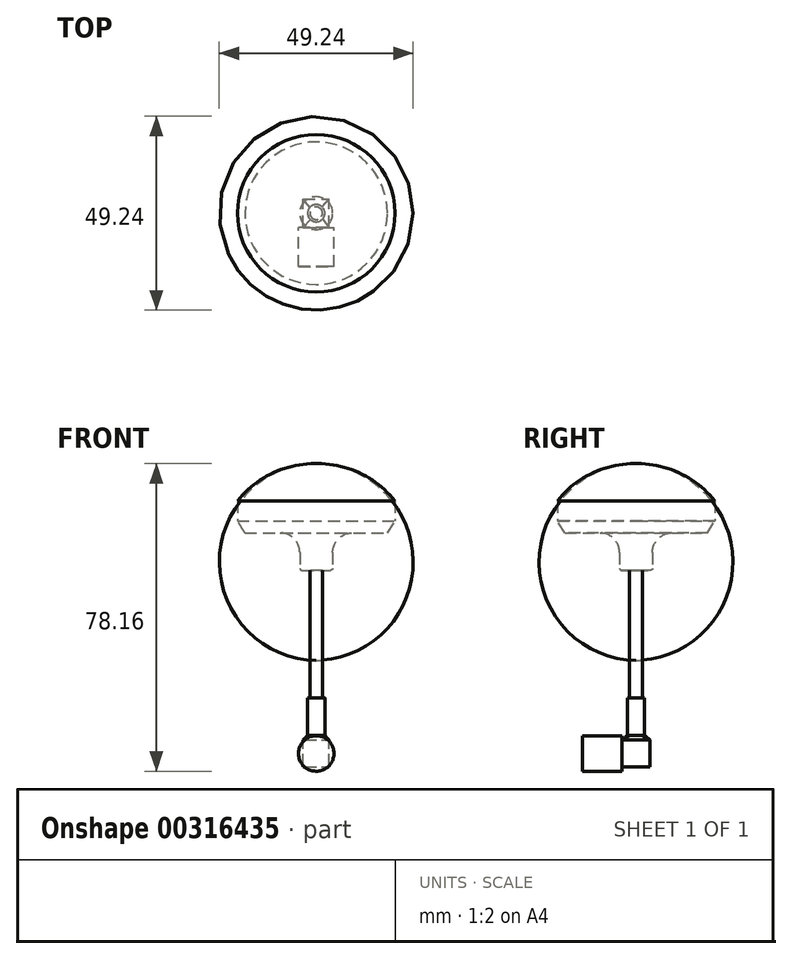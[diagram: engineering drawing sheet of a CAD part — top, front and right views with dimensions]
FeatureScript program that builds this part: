
annotation { "Feature Type Name" : "Feature", "Feature Type Description" : "" }
export const myFeature = defineFeature(function(context is Context, id is Id, definition is map)
    precondition{}
    {
        {
            var Q0;
            Q0=qCreatedBy(makeId("Right.planeOp"),FACE);
            var sketch = newSketch(context, id + "F0", { "sketchPlane" : qUnion([Q0])});
            skLineSegment(sketch, "E0", {"start": v(18.1, 0) * mm, "end": v(9.17, 0) * mm});
            skLineSegment(sketch, "E1", {"start": v(4.17, -5) * mm, "end": v(4.17, -9) * mm});
            skLineSegment(sketch, "E2", {"start": v(3.68, -9.5) * mm, "end": v(0, -9.5) * mm});
            skLineSegment(sketch, "E3", {"start": v(0, -9.5) * mm, "end": v(0, 17.6) * mm});
            skPoint(sketch, "E4.visualSharp", {"position": v(4.17, 0) * mm});
            skArc(sketch, "E4.filletArc", {"start": v(9.17, 0) * mm, "mid": v(5.64, -1.46) * mm, "end": v(4.17, -5) * mm});
            skLineSegment(sketch, "E5", {"start": v(18.1, 0) * mm, "end": v(20, 3) * mm});
            skLineSegment(sketch, "E6", {"start": v(20, 3) * mm, "end": v(20, 8.1) * mm});
            skArc(sketch, "E7", {"start": v(20, 8.1) * mm, "mid": v(11.1, 15.18) * mm, "end": v(0, 17.6) * mm});
            skPoint(sketch, "E8.visualSharp", {"position": v(4.17, -9.5) * mm});
            skArc(sketch, "E8.filletArc", {"start": v(3.68, -9.5) * mm, "mid": v(4.03, -9.35) * mm, "end": v(4.17, -9) * mm});
            skSolve(sketch);
        }
        {
            var Q0;
            Q0 = qSketchRegion(id + "F0", true);
            var Q1;
            Q1=sQuery(id+"F0.wireOp",EDGE,"E3");
            revolve(context, id + "F1", {"entities" : qUnion([Q0]), "axis" : qUnion([Q1]), "revolveType" : RevolveType.FULL});
        }
        {
            var Q0;
            Q0=makeQuery(id+"F1.opRevolve","SWEPT_FACE",FACE,{"disambiguationData":[OSD([sQuery(id+"F0.wireOp",EDGE,"E2")])]});
            var sketch = newSketch(context, id + "F2", { "sketchPlane" : qUnion([Q0])});
            skCircle(sketch, "E9", {"center": v(0, 0) * mm, "radius": 1.6 * mm});
            skSolve(sketch);
        }
        {
            var Q0;
            Q0 = qSketchRegion(id + "F2", true);
            extrude(context, id + "F3", {"entities" : qUnion([Q0]), "operationType" : NewBodyOperationType.ADD, "depth" : 32.4 * mm});
        }
        {
            var Q0;
            Q0=makeQuery(id+"F3.opExtrude","CAP_FACE",FACE,{"disambiguationData":[OSD([sQuery(id+"F2.wireOp",EDGE,"E9")])],"isStart":false});
            var sketch = newSketch(context, id + "F4", { "sketchPlane" : qUnion([Q0])});
            skCircle(sketch, "E10", {"center": v(0, 0) * mm, "radius": 2.2 * mm});
            skSolve(sketch);
        }
        {
            var Q0;
            Q0 = qSketchRegion(id + "F4", true);
            extrude(context, id + "F5", {"entities" : qUnion([Q0]), "operationType" : NewBodyOperationType.ADD, "depth" : 9.5 * mm});
        }
        {
            var Q0;
            Q0=makeQuery(id+"F5.opExtrude","CAP_FACE",FACE,{"disambiguationData":[OSD([sQuery(id+"F4.wireOp",EDGE,"E10")])],"isStart":false});
            cPlane(context, id + "F6", {"entities" : qUnion([Q0]), "cplaneType" : CPlaneType.OFFSET, "offset" : 1.25 * mm, "width" : 150 * mm, "height" : 150 * mm});
        }
        {
            var Q0;
            Q0=qCreatedBy(id+"F6.planeOp",FACE);
            var sketch = newSketch(context, id + "F7", { "sketchPlane" : qUnion([Q0])});
            skLineSegment(sketch, "E11.bottom", {"start": v(-3.3, 3.6) * mm, "end": v(3.3, 3.6) * mm});
            skLineSegment(sketch, "E11.top", {"start": v(-3.3, -3.6) * mm, "end": v(3.3, -3.6) * mm});
            skLineSegment(sketch, "E11.left", {"start": v(-3.3, 3.6) * mm, "end": v(-3.3, -3.6) * mm});
            skLineSegment(sketch, "E11.right", {"start": v(3.3, 3.6) * mm, "end": v(3.3, -3.6) * mm});
            skPoint(sketch, "E11.middle", {"position": v(0, 0) * mm});
            skSolve(sketch);
        }
        {
            var Q0;
            Q0 = qSketchRegion(id + "F7", true);
            extrude(context, id + "F8", {"entities" : qUnion([Q0]), "operationType" : NewBodyOperationType.ADD, "depth" : 6.8 * mm});
        }
        {
            var Q2;
            Q2=makeQuery(id+"F5.opExtrude","CAP_FACE",FACE,{"disambiguationData":[OSD([sQuery(id+"F4.wireOp",EDGE,"E10")])],"isStart":false});
            var Q3;
            Q3=makeQuery(id+"F8.opExtrude","CAP_FACE",FACE,{"disambiguationData":[OSD([sQuery(id+"F7.wireOp",EDGE,"E11.bottom"),sQuery(id+"F7.wireOp",EDGE,"E11.top"),sQuery(id+"F7.wireOp",EDGE,"E11.left"),sQuery(id+"F7.wireOp",EDGE,"E11.right")])],"isStart":true});
            loft(context, id + "F9", {"operationType" : NewBodyOperationType.ADD, "sheetProfilesArray" : [{ "sheetProfileEntities" : qUnion([Q2]) }, { "sheetProfileEntities" : qUnion([Q3]) }]});
        }
        {
            var Q0;
            Q0=makeQuery(id+"F8.opExtrude","SWEPT_FACE",FACE,{"disambiguationData":[OSD([sQuery(id+"F7.wireOp",EDGE,"E11.bottom")])]});
            var sketch = newSketch(context, id + "F10", { "sketchPlane" : qUnion([Q0])});
            skCircle(sketch, "E12", {"center": v(0, -56.05) * mm, "radius": 4.5 * mm});
            skLineSegment(sketch, "E13", {"start": v(0, -56.05) * mm, "end": v(0, -59.45) * mm, "construction": true});
            skLineSegment(sketch, "E14", {"start": v(0, -56.05) * mm, "end": v(0, -52.65) * mm, "construction": true});
            skSolve(sketch);
        }
        {
            var Q0;
            Q0 = qSketchRegion(id + "F10", true);
            extrude(context, id + "F11", {"entities" : qUnion([Q0]), "operationType" : NewBodyOperationType.ADD, "depth" : 10 * mm});
        }
    });
